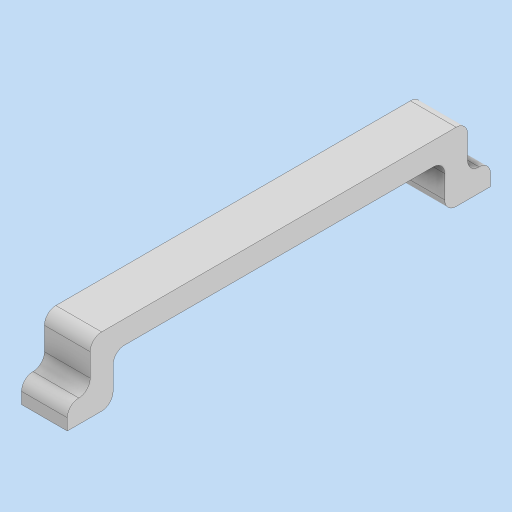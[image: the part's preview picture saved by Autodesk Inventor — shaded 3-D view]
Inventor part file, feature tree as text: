
AUTODESK INVENTOR PART (.ipt)
format: ipt  version: 2024 (Build 280153000, 153)  size: 150,016 bytes
history: native  units: mm
features: extrude x3, sketch x3, fillet x2
ambient origin geometry x8: Origin, YZ Plane, XZ Plane, XY Plane, X Axis, Y Axis, Z Axis, Center Point
bodies: Solid1 (feature_tree)
feature tree (8):
  extrude  "Extrusion1"  Depth=4.0mm
  extrude  "Extrusion2"  Depth=2.0mm
  extrude  "Extrusion3"  Depth=2.0mm TaperAngle=0.0deg
  fillet  "Fillet3"  Radius=2.0mm
  fillet  "Fillet4"  Radius=1.0mm
  sketch  "Sketch1"  dims[d0=37.0mm d1=4.0mm]
  sketch  "Sketch2"  dims[d2=2.0mm d3=0.0mm d4=2.0mm]
  sketch  "Sketch3"  dims[d5=2.0mm d6=2.0mm d7=0.0mm d10=2.0mm d11=0.0mm d12=1.0mm d13=1.0mm]
